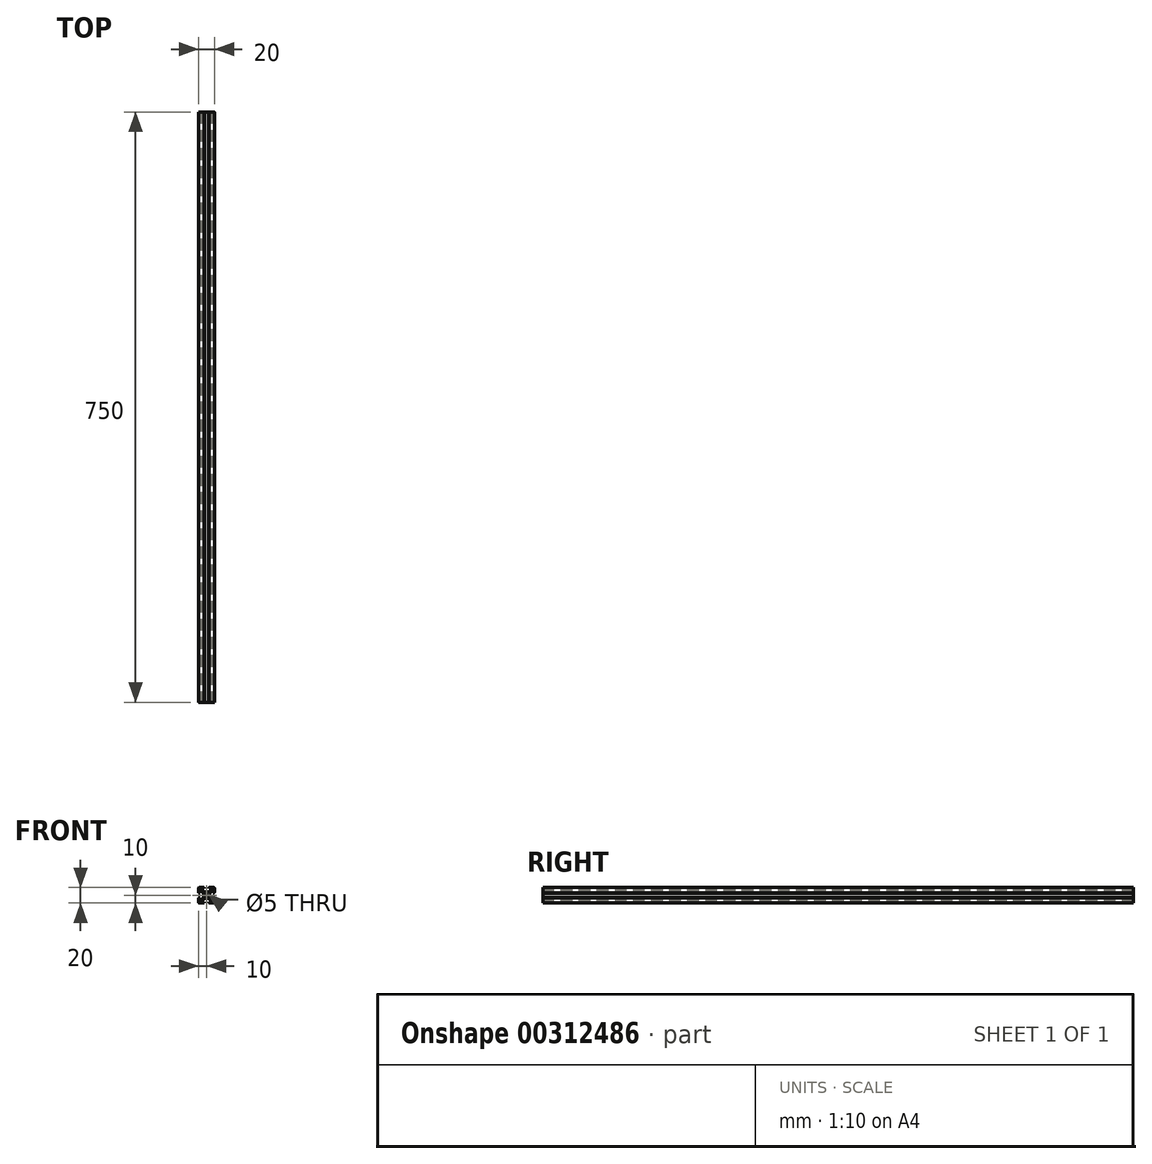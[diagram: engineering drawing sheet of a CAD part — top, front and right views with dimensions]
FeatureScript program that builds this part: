
annotation { "Feature Type Name" : "Feature", "Feature Type Description" : "" }
export const myFeature = defineFeature(function(context is Context, id is Id, definition is map)
    precondition{}
    {
        {
            var Q0;
            Q0=qCreatedBy(makeId("Front.planeOp"),FACE);
            var sketch = newSketch(context, id + "F0", { "sketchPlane" : qUnion([Q0])});
            skLineSegment(sketch, "E0.top", {"start": v(-3.6, 10) * mm, "end": v(-9, 10) * mm});
            skLineSegment(sketch, "E0.right", {"start": v(-10, 3.6) * mm, "end": v(-10, 9) * mm});
            skLineSegment(sketch, "E1", {"start": v(-3.1, 9.5) * mm, "end": v(-3.1, 8.46) * mm});
            skLineSegment(sketch, "E2", {"start": v(-3.1, 8.46) * mm, "end": v(-5.63, 8.46) * mm});
            skLineSegment(sketch, "E3", {"start": v(-5.63, 8.46) * mm, "end": v(-5.63, 6.92) * mm});
            skLineSegment(sketch, "E4", {"start": v(-5.63, 6.92) * mm, "end": v(-2.61, 3.9) * mm});
            skPoint(sketch, "E5.visualSharp", {"position": v(-3.1, 10) * mm});
            skArc(sketch, "E5.filletArc", {"start": v(-3.1, 9.5) * mm, "mid": v(-3.25, 9.85) * mm, "end": v(-3.6, 10) * mm});
            skLineSegment(sketch, "E6.MirrorCS", {"start": v(-6.92, 5.63) * mm, "end": v(-3.9, 2.61) * mm});
            skLineSegment(sketch, "E7.MirrorCS", {"start": v(-8.46, 3.1) * mm, "end": v(-8.46, 5.63) * mm});
            skLineSegment(sketch, "E8.MirrorCS", {"start": v(-9.5, 3.1) * mm, "end": v(-8.46, 3.1) * mm});
            skArc(sketch, "E9.MirrorCS", {"start": v(-9.5, 3.1) * mm, "mid": v(-9.85, 3.25) * mm, "end": v(-10, 3.6) * mm});
            skPoint(sketch, "E10.visualSharp", {"position": v(-10, 10) * mm});
            skArc(sketch, "E10.filletArc", {"start": v(-9, 10) * mm, "mid": v(-9.7, 9.7) * mm, "end": v(-10, 9) * mm});
            skLineSegment(sketch, "E11.MirrorCS", {"start": v(6.92, 5.63) * mm, "end": v(3.9, 2.61) * mm});
            skLineSegment(sketch, "E12.MirrorCS", {"start": v(8.46, 3.1) * mm, "end": v(8.46, 5.63) * mm});
            skLineSegment(sketch, "E13.MirrorCS", {"start": v(9.5, 3.1) * mm, "end": v(8.46, 3.1) * mm});
            skArc(sketch, "E14.MirrorCS", {"start": v(9.5, 3.1) * mm, "mid": v(9.85, 3.25) * mm, "end": v(10, 3.6) * mm});
            skLineSegment(sketch, "E15.MirrorCS", {"start": v(10, 3.6) * mm, "end": v(10, 9) * mm});
            skArc(sketch, "E16.MirrorCS", {"start": v(9, 10) * mm, "mid": v(9.7, 9.7) * mm, "end": v(10, 9) * mm});
            skLineSegment(sketch, "E17.MirrorCS", {"start": v(3.6, 10) * mm, "end": v(9, 10) * mm});
            skArc(sketch, "E18.MirrorCS", {"start": v(3.1, 9.5) * mm, "mid": v(3.25, 9.85) * mm, "end": v(3.6, 10) * mm});
            skLineSegment(sketch, "E19.MirrorCS", {"start": v(3.1, 9.5) * mm, "end": v(3.1, 8.46) * mm});
            skLineSegment(sketch, "E20.MirrorCS", {"start": v(3.1, 8.46) * mm, "end": v(5.63, 8.46) * mm});
            skLineSegment(sketch, "E21.MirrorCS", {"start": v(5.63, 6.92) * mm, "end": v(2.61, 3.9) * mm});
            skPoint(sketch, "E22.orphan", {"position": v(-6.92, 5.63) * mm});
            skPoint(sketch, "E23.MirrorCS.end.orphan", {"position": v(-10, 5.63) * mm});
            skLineSegment(sketch, "E24", {"start": v(-8.46, 5.63) * mm, "end": v(-6.92, 5.63) * mm});
            skPoint(sketch, "E25.MirrorCS.start.orphan", {"position": v(5.63, 6.92) * mm});
            skPoint(sketch, "E26.orphan", {"position": v(6.92, 5.63) * mm});
            skPoint(sketch, "E27.MirrorCS.end.orphan", {"position": v(10, 5.63) * mm});
            skLineSegment(sketch, "E28.MirrorCS", {"start": v(5.63, 8.46) * mm, "end": v(5.63, 6.92) * mm});
            skLineSegment(sketch, "E29.MirrorCS", {"start": v(8.46, 5.63) * mm, "end": v(6.92, 5.63) * mm});
            skLineSegment(sketch, "E30.MirrorCS", {"start": v(6.92, -5.63) * mm, "end": v(3.9, -2.61) * mm});
            skLineSegment(sketch, "E31.MirrorCS", {"start": v(5.63, -6.92) * mm, "end": v(2.61, -3.9) * mm});
            skLineSegment(sketch, "E32.MirrorCS", {"start": v(-5.63, -6.92) * mm, "end": v(-2.61, -3.9) * mm});
            skLineSegment(sketch, "E33.MirrorCS", {"start": v(-6.92, -5.63) * mm, "end": v(-3.9, -2.61) * mm});
            skLineSegment(sketch, "E34.MirrorCS", {"start": v(-8.46, -3.1) * mm, "end": v(-8.46, -5.63) * mm});
            skLineSegment(sketch, "E35.MirrorCS", {"start": v(-9.5, -3.1) * mm, "end": v(-8.46, -3.1) * mm});
            skArc(sketch, "E36.MirrorCS", {"start": v(-9.5, -3.1) * mm, "mid": v(-9.85, -3.25) * mm, "end": v(-10, -3.6) * mm});
            skLineSegment(sketch, "E37.MirrorCS", {"start": v(-10, -3.6) * mm, "end": v(-10, -9) * mm});
            skLineSegment(sketch, "E38.MirrorCS", {"start": v(8.46, -5.63) * mm, "end": v(6.92, -5.63) * mm});
            skLineSegment(sketch, "E39.MirrorCS", {"start": v(8.46, -3.1) * mm, "end": v(8.46, -5.63) * mm});
            skLineSegment(sketch, "E40.MirrorCS", {"start": v(9.5, -3.1) * mm, "end": v(8.46, -3.1) * mm});
            skArc(sketch, "E41.MirrorCS", {"start": v(9.5, -3.1) * mm, "mid": v(9.85, -3.25) * mm, "end": v(10, -3.6) * mm});
            skLineSegment(sketch, "E42.MirrorCS", {"start": v(10, -3.6) * mm, "end": v(10, -9) * mm});
            skLineSegment(sketch, "E43.MirrorCS", {"start": v(-8.46, -5.63) * mm, "end": v(-6.92, -5.63) * mm});
            skLineSegment(sketch, "E44.MirrorCS", {"start": v(-5.63, -8.46) * mm, "end": v(-5.63, -6.92) * mm});
            skLineSegment(sketch, "E45.MirrorCS", {"start": v(-3.1, -8.46) * mm, "end": v(-5.63, -8.46) * mm});
            skLineSegment(sketch, "E46.MirrorCS", {"start": v(-3.1, -9.5) * mm, "end": v(-3.1, -8.46) * mm});
            skLineSegment(sketch, "E47.MirrorCS", {"start": v(-3.6, -10) * mm, "end": v(-9, -10) * mm});
            skLineSegment(sketch, "E48.MirrorCS", {"start": v(3.1, -9.5) * mm, "end": v(3.1, -8.46) * mm});
            skArc(sketch, "E49.MirrorCS", {"start": v(3.1, -9.5) * mm, "mid": v(3.25, -9.85) * mm, "end": v(3.6, -10) * mm});
            skLineSegment(sketch, "E50.MirrorCS", {"start": v(3.6, -10) * mm, "end": v(9, -10) * mm});
            skLineSegment(sketch, "E51.MirrorCS", {"start": v(3.1, -8.46) * mm, "end": v(5.63, -8.46) * mm});
            skLineSegment(sketch, "E52.MirrorCS", {"start": v(5.63, -8.46) * mm, "end": v(5.63, -6.92) * mm});
            skArc(sketch, "E53.MirrorCS", {"start": v(9, -10) * mm, "mid": v(9.7, -9.7) * mm, "end": v(10, -9) * mm});
            skArc(sketch, "E54.MirrorCS", {"start": v(-9, -10) * mm, "mid": v(-9.7, -9.7) * mm, "end": v(-10, -9) * mm});
            skArc(sketch, "E55.MirrorCS", {"start": v(-3.1, -9.5) * mm, "mid": v(-3.25, -9.85) * mm, "end": v(-3.6, -10) * mm});
            skPoint(sketch, "E56.MirrorCS.start.orphan", {"position": v(-3.9, 2.61) * mm});
            skPoint(sketch, "E57.MirrorCS.start.orphan", {"position": v(-3.9, -2.61) * mm});
            skPoint(sketch, "E58.MirrorCS.start.orphan", {"position": v(2.61, 3.9) * mm});
            skPoint(sketch, "E59.MirrorCS.start.orphan", {"position": v(3.9, 2.61) * mm});
            skPoint(sketch, "E60.MirrorCS.start.orphan", {"position": v(3.9, -2.61) * mm});
            skPoint(sketch, "E61.MirrorCS.start.orphan", {"position": v(2.61, -3.9) * mm});
            skPoint(sketch, "E62.MirrorCS.start.orphan", {"position": v(-2.61, -3.9) * mm});
            skLineSegment(sketch, "E63", {"start": v(-3.9, 2.61) * mm, "end": v(-3.9, -2.61) * mm});
            skLineSegment(sketch, "E64", {"start": v(-2.61, 3.9) * mm, "end": v(2.61, 3.9) * mm});
            skLineSegment(sketch, "E65", {"start": v(3.9, 2.61) * mm, "end": v(3.9, -2.61) * mm});
            skLineSegment(sketch, "E66", {"start": v(-2.61, -3.9) * mm, "end": v(2.61, -3.9) * mm});
            skCircle(sketch, "E67", {"center": v(0, 0) * mm, "radius": 2.5 * mm});
            skSolve(sketch);
        }
        {
            var Q0;
            Q0=qSketchRegion(id+"F0",true);
            extrude(context, id + "F1", {"entities" : qUnion([Q0]), "oppositeDirection" : true, "depth" : 750 * mm});
        }
    });
